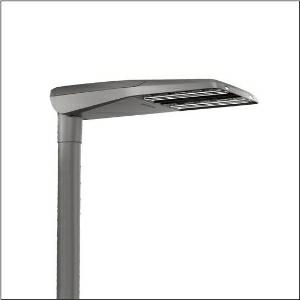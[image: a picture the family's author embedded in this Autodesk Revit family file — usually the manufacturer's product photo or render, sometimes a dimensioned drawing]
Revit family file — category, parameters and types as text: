
# Revit family: streetlight_sl_11_iq_midi___st1_2a_5xc3a41e08le_4284
name_source: partatom
category: Lighting Fixtures
units: mm (PartAtom-declared; Revit-internal decimal feet)

## family parameters
Cut with Voids When Loaded = No
Host = Face
Light Source = No
Part Type = Normal
Room Calculation Point = No
Round Connector Dimension = Use Diameter
Shared = No

## types (1)
- --- (1 x LED, 9590 lm, 60.4 W, 4000K)
    Apparent Load = 60 VA
    CIE Flux Codes = 32 70 96 100 100
    Color Rendering = 70
    Color Temperature = 4000K
    Default Elevation = 1800 mm
    Description = Streetlight SL 11 iQ midi, mast luminaire, primary light control with 3 zone facetted reflector, of plastic, silver coated, highly specular, primary optical cover: cover, of PMMA, transparent, light distribution: ST1.2a, light emission: direct distribution, primary light characteristic: asymmetric, installation type: post-top, side-entry, lamps: LED, High Power LED, rated values: 9.590lm | 60,4W | 158,8lm/W (begin service life); end service life: 9.590lm | 62,5W; at 50% lumin. flux: 4.795lm | 29,7W | 161,4lm/W, colour temperature: 4000K, colour rendering: CRI > 70, light colour: 740, light setting 1 begin service life: 100% | 9.590lm | 60,4W | 158,8lm/W | 4.000K, light setting 1 end service life: 62,5W, further light settings possible, control: optimised constant luminous flux control (CLO 2.0), Desk-Remote (wireless, voltage-free reading and setting of iQ features in the workshop via application-optimized NFC function/RFID function), Light-Fading, Smart-Wire, Night-Set, Lumen-Switch, Temp-Guard, Auto-Match, with cable H07RN-F 3x 1.5mm², mains connection: 230..240V, AC, 50/60Hz, connection cable pre-assembled, cable length: 8,5m, luminaire housing, of diecast aluminium, powder-coated, SITECO metallic grey (DB 702S), please order mast flange separately, inclination adjustable without tools: 0°, 5°, 10°, 15° (post-top) | 0°, -5°, -10°, -15° (side-entry), sealing non-destructively replaceable, multi-level sealing system, length: 780mm, width: 376mm, height: 118mm, mast flange for spigot size: 42mm (side-entry): 5XC10008XM4, 60/48mm (side-entry/post-top): 5XC10108XM2, 76/60mm (side-entry/post-top): 5XC10108XM1, equipment: standard, protection rating (complete): IP66, insulation class (complete): insulation class II (safety insulation), certification: CE, ENEC, ENEC+, VDE, impact resistance: IK10, permissible operating ambient temperature for outdoor applications: -25..+50°C, standard-compliant lighting for roads and squares, Environmental Product Declaration (EPD) tested and certified by an independent institute, packaging unit: 1 piece

Light Distribution: ST1.2a
    Height = 118 mm
    Lamp = 1 x LED
    Lamp Light Flux = 9590 lm
    Lamp Power = 60.4 W
    Lamp count = 1
    Length = 780 mm
    Luminous efficacy = 159 lm/W
    Manufacturer = Siteco
    ModVariant = No
    Model = 5XC3A41E08LE
    Number of Poles = 1
    OnlyDefault = Yes
    Power Factor = 1
    Product Name = Streetlight SL 11 iQ midi | ST1.2a
    Product group = mast luminaire | pylon top
    ProductGroupID = 6100
    Protection Class = Protection class II
    Protection Degree = IP 66
    RLX_Detail_Level = 1
    RLX_Emergency_Light_Flux = 0 lm
    RLX_Emergency_Type = 0
    RLX_Emergency_Type_DB = No
    RlxData = <blob elided: 70817 chars, md5=caa339f2>
    Socket = socket
    Standby Power = 0 W
    System Light Flux = 9590 lm
    System Power = 60 W
    Type Comments = factory setting: luminous flux: 100 % | dim-lin: 254 | 520 mA
    Type Image = l_1005960.jpg
    URL = http://relux.com
    VarID = @adj_194521
    Voltage = 0 V
    Weight = 0.00 kg
    Width = 376 mm

## geometry (parser evidence)
native form markers: Blend x4, Sweep x10
no freeform markers — native parametric forms only
